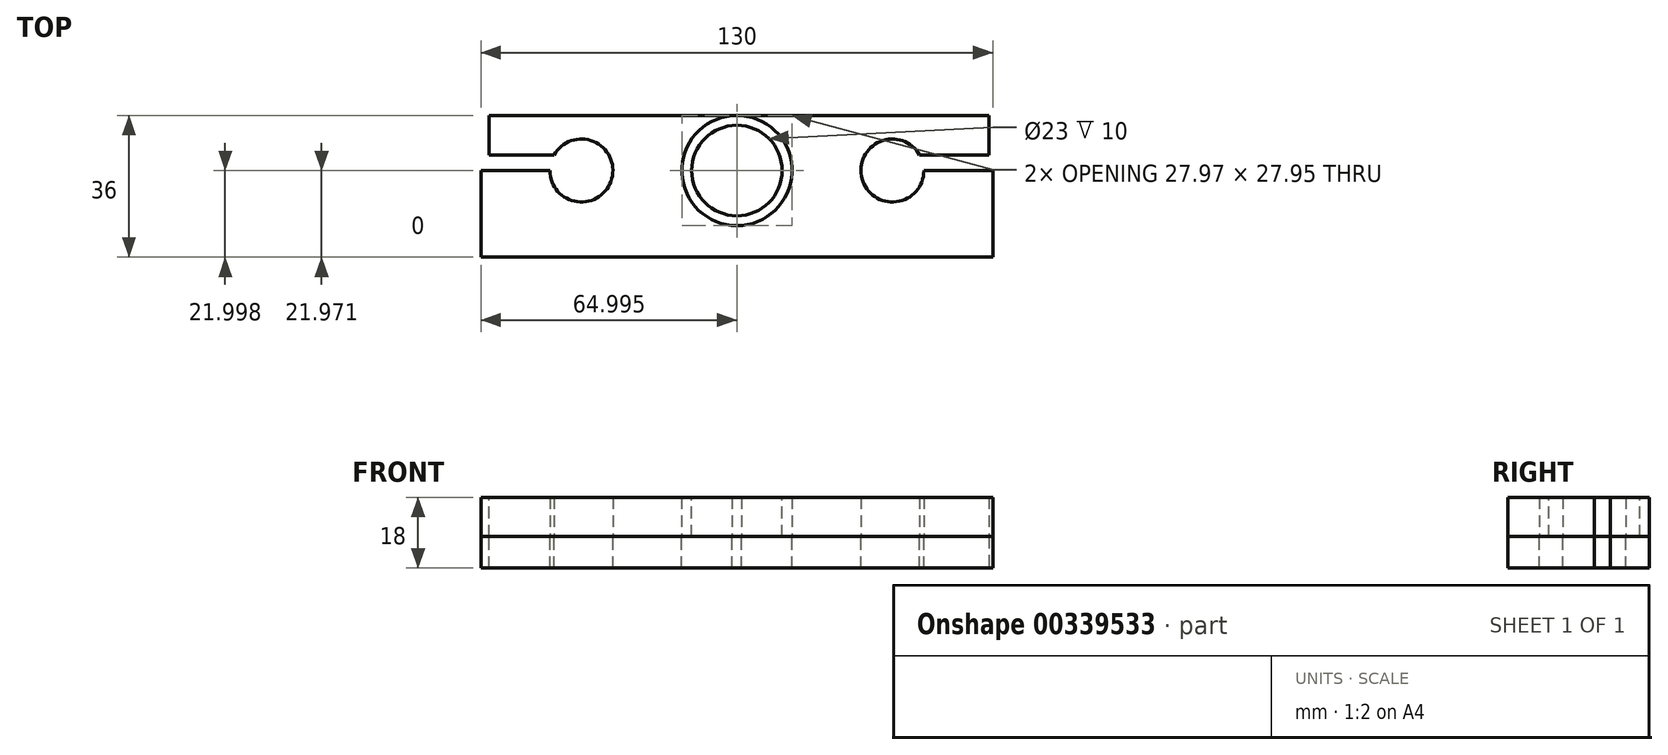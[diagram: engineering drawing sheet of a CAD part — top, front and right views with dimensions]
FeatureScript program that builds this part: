
annotation { "Feature Type Name" : "Feature", "Feature Type Description" : "" }
export const myFeature = defineFeature(function(context is Context, id is Id, definition is map)
    precondition{}
    {
        {
            var Q0;
            Q0=qCreatedBy(makeId("Top.planeOp"),FACE);
            var sketch = newSketch(context, id + "F0", { "sketchPlane" : qUnion([Q0])});
            skLineSegment(sketch, "E0.bottom", {"start": v(-114.47, 32.47) * mm, "end": v(15.53, 32.47) * mm});
            skLineSegment(sketch, "E0.top", {"start": v(-114.47, -3.53) * mm, "end": v(15.53, -3.53) * mm});
            skLineSegment(sketch, "E0.left", {"start": v(-114.47, 32.47) * mm, "end": v(-114.47, -3.53) * mm});
            skLineSegment(sketch, "E0.right", {"start": v(15.53, 32.47) * mm, "end": v(15.53, -3.53) * mm});
            skCircle(sketch, "E1", {"center": v(-88.97, 18.47) * mm, "radius": 8 * mm});
            skCircle(sketch, "E2", {"center": v(-9.97, 18.47) * mm, "radius": 8 * mm});
            skCircle(sketch, "E3", {"center": v(-49.47, 18.47) * mm, "radius": 14 * mm});
            skPoint(sketch, "E3.centerSnap0", {"position": v(-49.47, -3.53) * mm});
            skLineSegment(sketch, "E4", {"start": v(-88.97, 18.47) * mm, "end": v(-114.47, 18.47) * mm});
            skLineSegment(sketch, "E5", {"start": v(-9.97, 18.47) * mm, "end": v(15.53, 18.47) * mm});
            skLineSegment(sketch, "E6", {"start": v(15.53, 22.47) * mm, "end": v(-11.45, 22.47) * mm});
            skLineSegment(sketch, "E7", {"start": v(-114.47, 22.47) * mm, "end": v(-88.97, 22.47) * mm});
            skLineSegment(sketch, "E8", {"start": v(-50.7, 32.41) * mm, "end": v(-48.25, 32.41) * mm});
            skSolve(sketch);
        }
        {
            var Q0;
            {var subQ9=sQuery(id+"F0.wireOp",EDGE,"E0.bottom");Q0=makeQuery(id+"F0.imprint","IMPRINT",FACE,{"disambiguationData":[TD([[makeQuery(id+"F0.imprint","IMPRINT",EDGE,{"derivedFrom":subQ9}),-1.0]])]});}
            var Q1;
            Q1=makeQuery(id+"F0.imprint","IMPRINT",FACE,{"disambiguationData":[TD([[makeQuery(id+"F0.imprint","IMPRINT",EDGE,{"derivedFrom":sQuery(id+"F0.wireOp",EDGE,"E3")}),1.0]])]});
            extrude(context, id + "F1", {"entities" : qUnion([Q0, Q1]), "oppositeDirection" : true, "depth" : 8 * mm});
        }
        {
            var Q0;
            {var subQ0=sQuery(id+"F0.wireOp",EDGE,"E8");Q0=makeQuery(id+"F0.imprint","IMPRINT",FACE,{"disambiguationData":[TD([[makeQuery(id+"F0.imprint","IMPRINT",EDGE,{"derivedFrom":subQ0}),-1.0]])]});}
            extrude(context, id + "F2", {"entities" : qUnion([Q0]), "depth" : 10 * mm});
        }
        {
            var Q0;
            Q0=makeQuery(id+"F1.opExtrude","CAP_FACE",FACE,{"disambiguationData":[OSD([sQuery(id+"F0.wireOp",EDGE,"E0.bottom"),sQuery(id+"F0.wireOp",EDGE,"E0.top"),sQuery(id+"F0.wireOp",EDGE,"E0.left"),sQuery(id+"F0.wireOp",EDGE,"E0.right"),sQuery(id+"F0.wireOp",EDGE,"E1"),sQuery(id+"F0.wireOp",EDGE,"E2"),sQuery(id+"F0.wireOp",EDGE,"E3"),sQuery(id+"F0.wireOp",EDGE,"E4"),sQuery(id+"F0.wireOp",EDGE,"E5"),sQuery(id+"F0.wireOp",EDGE,"E6"),sQuery(id+"F0.wireOp",EDGE,"E7"),sQuery(id+"F0.wireOp",EDGE,"E8")])],"isStart":true});
            extrude(context, id + "F3", {"entities" : qUnion([Q0]), "depth" : 10 * mm});
        }
        {
            var Q0;
            Q0=sQuery(id+"F0.wireOp",VERTEX,"E3.center");
            var Q1;
            Q1=makeQuery(id+"F2.opExtrude","SWEPT_BODY",BODY,{"disambiguationData":[OSD([sQuery(id+"F0.wireOp",EDGE,"E3"),sQuery(id+"F0.wireOp",EDGE,"E8")])]});
            hole(context, id + "F4", {"style" : HoleStyle.SIMPLE, "endStyle" : HoleEndStyle.THROUGH, "oppositeDirection" : true, "holeDiameter" : 23 * mm, "isTappedThrough" : true, "tappedDepth" : 12 * mm, "tapClearance" : 3, "locations" : qUnion([Q0]), "scope" : qUnion([Q1])});
        }
        {
            var Q0;
            {var subQ0=sQuery(id+"F0.wireOp",EDGE,"E0.right");Q0=makeQuery(id+"F3.opExtrude","SWEPT_FACE",FACE,{"disambiguationData":[OSD([subQ0]),TDD([makeQuery(id+"F1.opExtrude","CAP_EDGE",EDGE,{"disambiguationData":[OSD([subQ0]),TDD([makeQuery(id+"F0.imprint","IMPRINT",EDGE,{"disambiguationData":[TD([[makeQuery(id+"F0.imprint","INTERSECT",VERTEX,{"derivedFrom":[sQuery(id+"F0.wireOp",EDGE,"E0.bottom"),subQ0]}),-1.0]])],"derivedFrom":subQ0})])],"isStart":true})])]});}
            var Q1;
            {var subQ0=sQuery(id+"F0.wireOp",EDGE,"E0.right");Q1=makeQuery(id+"F1.opExtrude","SWEPT_FACE",FACE,{"disambiguationData":[OSD([subQ0]),TDD([makeQuery(id+"F0.imprint","IMPRINT",EDGE,{"disambiguationData":[TD([[makeQuery(id+"F0.imprint","INTERSECT",VERTEX,{"derivedFrom":[sQuery(id+"F0.wireOp",EDGE,"E0.bottom"),subQ0]}),-1.0]])],"derivedFrom":subQ0})])]});}
            extrude(context, id + "F5", {"entities" : qUnion([Q0, Q1]), "operationType" : NewBodyOperationType.REMOVE, "oppositeDirection" : true, "depth" : 2 * mm, "symmetric" : true});
        }
        {
            var Q0;
            {var subQ0=sQuery(id+"F0.wireOp",EDGE,"E0.left");Q0=makeQuery(id+"F1.opExtrude","SWEPT_FACE",FACE,{"disambiguationData":[OSD([subQ0]),TDD([makeQuery(id+"F0.imprint","IMPRINT",EDGE,{"disambiguationData":[TD([[makeQuery(id+"F0.imprint","INTERSECT",VERTEX,{"derivedFrom":[sQuery(id+"F0.wireOp",EDGE,"E0.bottom"),subQ0]}),-1.0]])],"derivedFrom":subQ0})])]});}
            var Q1;
            {var subQ0=sQuery(id+"F0.wireOp",EDGE,"E0.left");Q1=makeQuery(id+"F3.opExtrude","SWEPT_FACE",FACE,{"disambiguationData":[OSD([subQ0]),TDD([makeQuery(id+"F1.opExtrude","CAP_EDGE",EDGE,{"disambiguationData":[OSD([subQ0]),TDD([makeQuery(id+"F0.imprint","IMPRINT",EDGE,{"disambiguationData":[TD([[makeQuery(id+"F0.imprint","INTERSECT",VERTEX,{"derivedFrom":[sQuery(id+"F0.wireOp",EDGE,"E0.bottom"),subQ0]}),-1.0]])],"derivedFrom":subQ0})])],"isStart":true})])]});}
            extrude(context, id + "F6", {"entities" : qUnion([Q0, Q1]), "operationType" : NewBodyOperationType.REMOVE, "oppositeDirection" : true, "depth" : 2 * mm});
        }
    });
